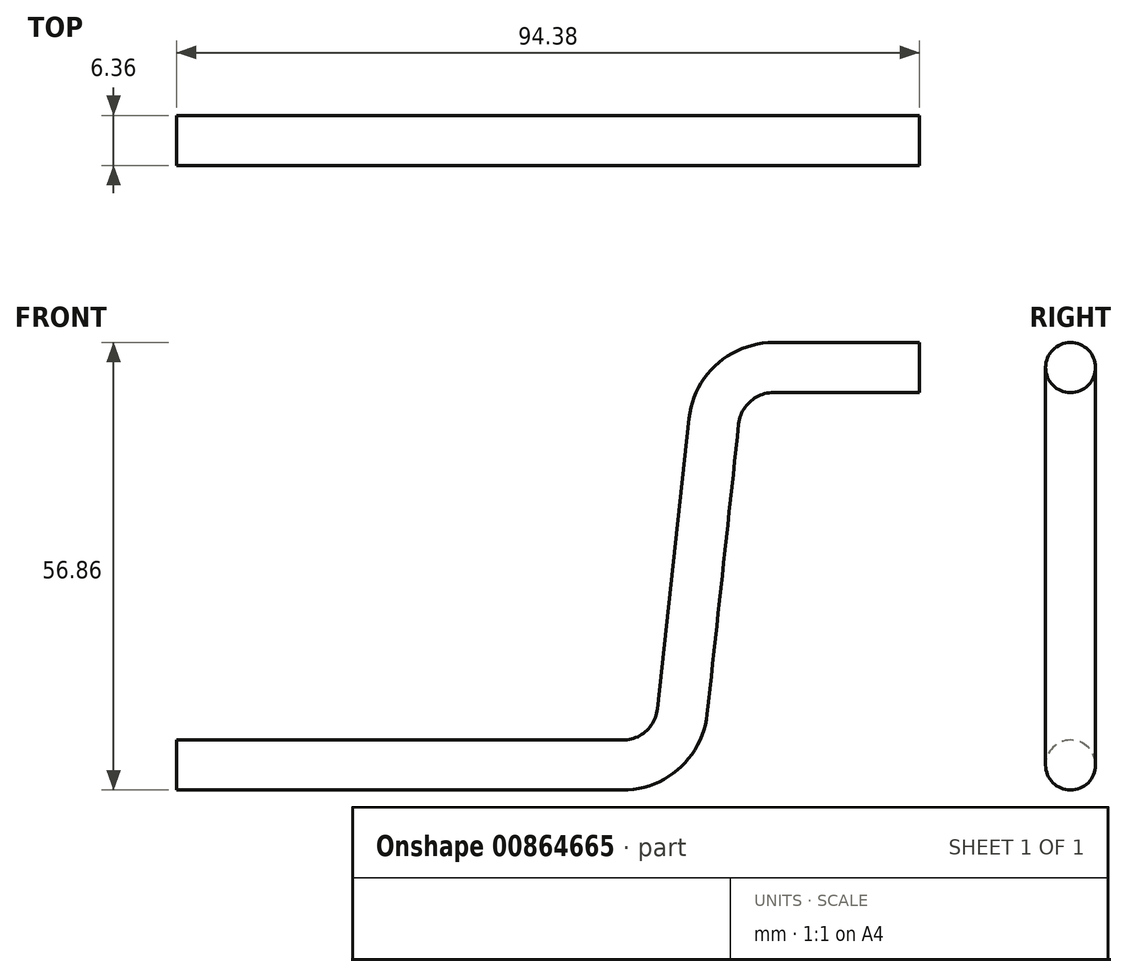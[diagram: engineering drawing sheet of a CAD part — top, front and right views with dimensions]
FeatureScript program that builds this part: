
annotation { "Feature Type Name" : "Feature", "Feature Type Description" : "" }
export const myFeature = defineFeature(function(context is Context, id is Id, definition is map)
    precondition{}
    {
        {
            var Q0;
            Q0=qCreatedBy(makeId("Right.planeOp"),FACE);
            var sketch = newSketch(context, id + "F0", { "sketchPlane" : qUnion([Q0])});
            skCircle(sketch, "E0", {"center": v(0, 0) * mm, "radius": 3.18 * mm});
            skSolve(sketch);
        }
        {
            var Q0;
            Q0=qCreatedBy(makeId("Front.planeOp"),FACE);
            var sketch = newSketch(context, id + "F1", { "sketchPlane" : qUnion([Q0])});
            skLineSegment(sketch, "E1", {"start": v(0, 0) * mm, "end": v(56.66, 0) * mm});
            skLineSegment(sketch, "E2", {"start": v(64.24, 6.8) * mm, "end": v(68.25, 43.7) * mm});
            skLineSegment(sketch, "E3", {"start": v(75.82, 50.5) * mm, "end": v(94.38, 50.5) * mm});
            skPoint(sketch, "E4.visualSharp", {"position": v(68.98, 50.5) * mm});
            skArc(sketch, "E4.filletArc", {"start": v(75.82, 50.5) * mm, "mid": v(70.73, 48.55) * mm, "end": v(68.25, 43.7) * mm});
            skPoint(sketch, "E5.visualSharp", {"position": v(63.5, 0) * mm});
            skArc(sketch, "E5.filletArc", {"start": v(56.66, 0) * mm, "mid": v(61.75, 1.95) * mm, "end": v(64.24, 6.8) * mm});
            skSolve(sketch);
        }
        {
            var Q0;
            Q0=makeQuery(id+"F0.imprint","IMPRINT",FACE,{"disambiguationData":[TD([[makeQuery(id+"F0.imprint","IMPRINT",EDGE,{"derivedFrom":sQuery(id+"F0.wireOp",EDGE,"E0")}),1.0]])]});
            var Q1;
            Q1 = qConstructionFilter(qBodyType(qCreatedBy(id + "F1" ,EDGE), BodyType.WIRE), ConstructionObject.NO);
            sweep(context, id + "F2", {"profiles" : qUnion([Q0]), "path" : qUnion([Q1])});
        }
    });
